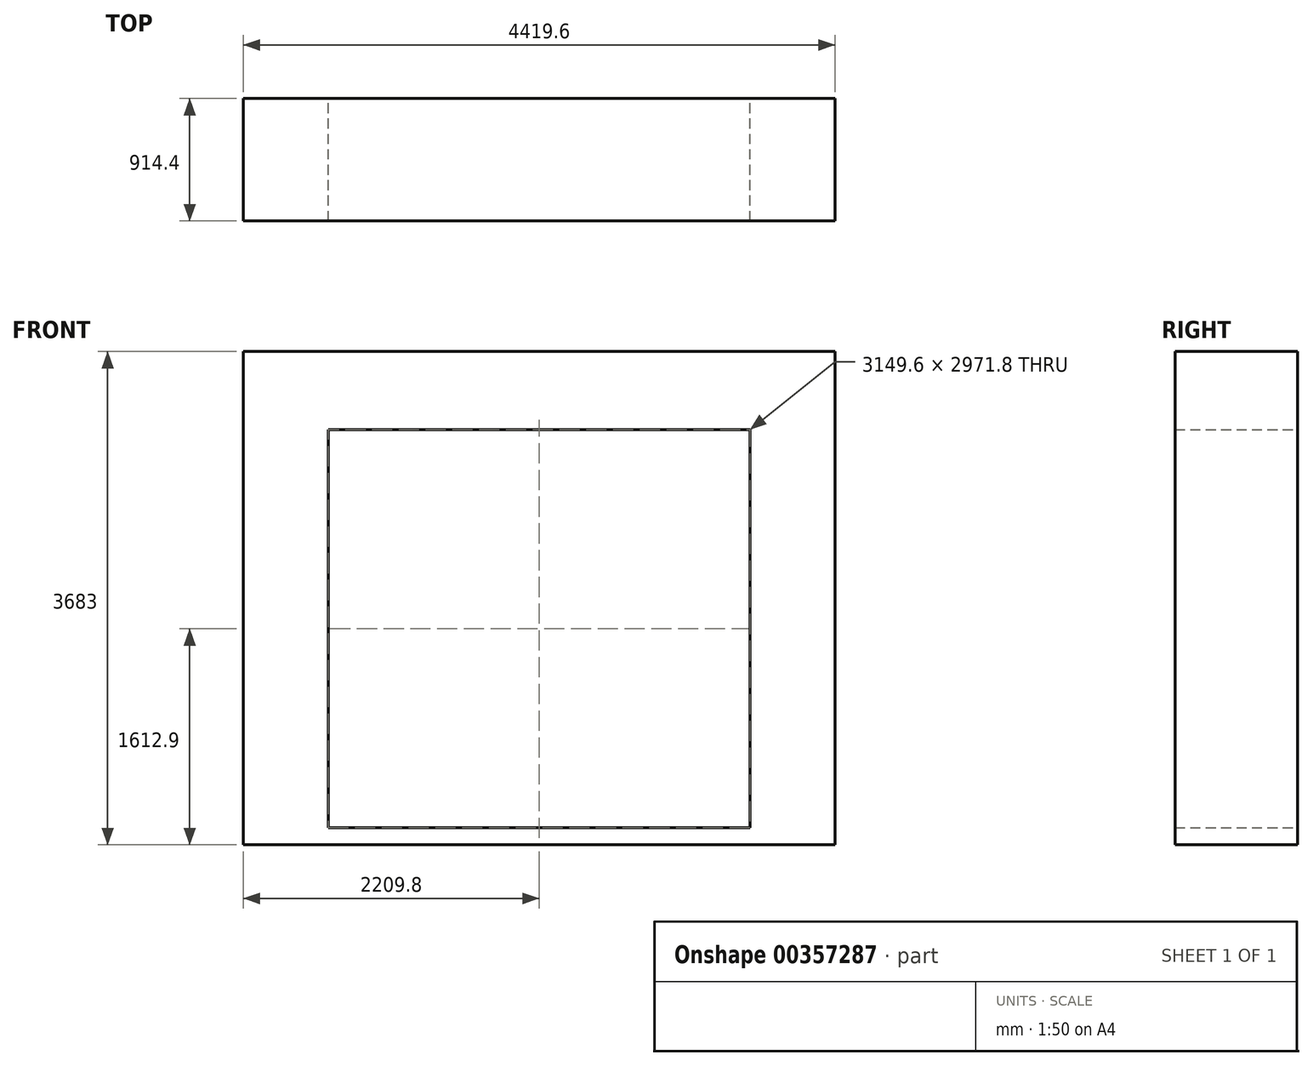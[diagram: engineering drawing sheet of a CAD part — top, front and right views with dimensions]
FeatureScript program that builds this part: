
annotation { "Feature Type Name" : "Feature", "Feature Type Description" : "" }
export const myFeature = defineFeature(function(context is Context, id is Id, definition is map)
    precondition{}
    {
        {
            var Q0;
            Q0=qCreatedBy(makeId("Front.planeOp"),FACE);
            var sketch = newSketch(context, id + "F0", { "sketchPlane" : qUnion([Q0])});
            skLineSegment(sketch, "E0", {"start": v(0, 0) * mm, "end": v(-4419.6, 0) * mm});
            skLineSegment(sketch, "E1", {"start": v(-4419.6, 0) * mm, "end": v(-4419.6, 3683) * mm});
            skLineSegment(sketch, "E2", {"start": v(-4419.6, 3683) * mm, "end": v(0, 3683) * mm});
            skLineSegment(sketch, "E3", {"start": v(0, 3683) * mm, "end": v(0, 0) * mm});
            skLineSegment(sketch, "E4.bottom", {"start": v(-3784.6, 3098.8) * mm, "end": v(-635, 3098.8) * mm});
            skLineSegment(sketch, "E4.top", {"start": v(-3784.6, 127) * mm, "end": v(-635, 127) * mm});
            skLineSegment(sketch, "E4.left", {"start": v(-3784.6, 3098.8) * mm, "end": v(-3784.6, 127) * mm});
            skLineSegment(sketch, "E4.right", {"start": v(-635, 3098.8) * mm, "end": v(-635, 127) * mm});
            skPoint(sketch, "E5", {"position": v(-2209.8, 3683) * mm});
            skSolve(sketch);
        }
        {
            var Q0;
            Q0=makeQuery(id+"F0.imprint","IMPRINT",FACE,{"disambiguationData":[TD([[makeQuery(id+"F0.imprint","IMPRINT",EDGE,{"derivedFrom":sQuery(id+"F0.wireOp",EDGE,"E0")}),-1.0]])]});
            extrude(context, id + "F1", {"entities" : qUnion([Q0]), "depth" : 914.4 * mm});
        }
    });
